# Revit family: SLC-6610
name_source: partatom
category: Pipe Accessories
units: mm (PartAtom-declared; Revit-internal decimal feet)

## family parameters
Cut with Voids When Loaded = No
Host = Face
OmniClass Number = 23.65.55.00
OmniClass Title = Distribution of Supplied Liquids/Gases
Part Type = Normal
Round Connector Dimension = Use Radius
Shared = No

## types (6) — shared parameters
Date Modified = January 30, 2015
Description = Not Available
Equipment Abbreviation = SH
Family Version = 1.0
Manufacturer = Symmons Industries, Inc.
Model = Not Available
Model Disclaimer = Contact Symmons Industries, Inc. For More Information
Product Page URL = http://www.symmons.com
URL = http://www.symmons.com
z GPM GPM = 0.000 GPM
zero-valued in all types: Default Elevation, z GPM Number, z Type Finish, z Type Flow Restrictor, z Type GPM

## per-type parameters (varying)
| type | Gallons Per Minute | Product Material |
| 0.5 GPM Flow Restrictor, Chrome | 0.500 GPM | Chrome - Symmons - Polished |
| 0.5 GPM Flow Restrictor, Satin Nickel | 0.500 GPM | Nickel - Symmons - Satin |
| 1.0 GPM Flow Restrictor, Chrome | 1.000 GPM | Chrome - Symmons - Polished |
| 1.5 GPM Flow Restrictor, Satin Nickel | 1.500 GPM | Nickel - Symmons - Satin |
| 1.0 Flow Restrictor, Satin Nickel | 1.000 GPM | Nickel - Symmons - Satin |
| 1.5 Flow Restrictor, Chrome | 1.500 GPM | Chrome - Symmons - Polished |

## geometry (parser evidence)
native form markers: Sweep x3
no freeform markers — native parametric forms only
